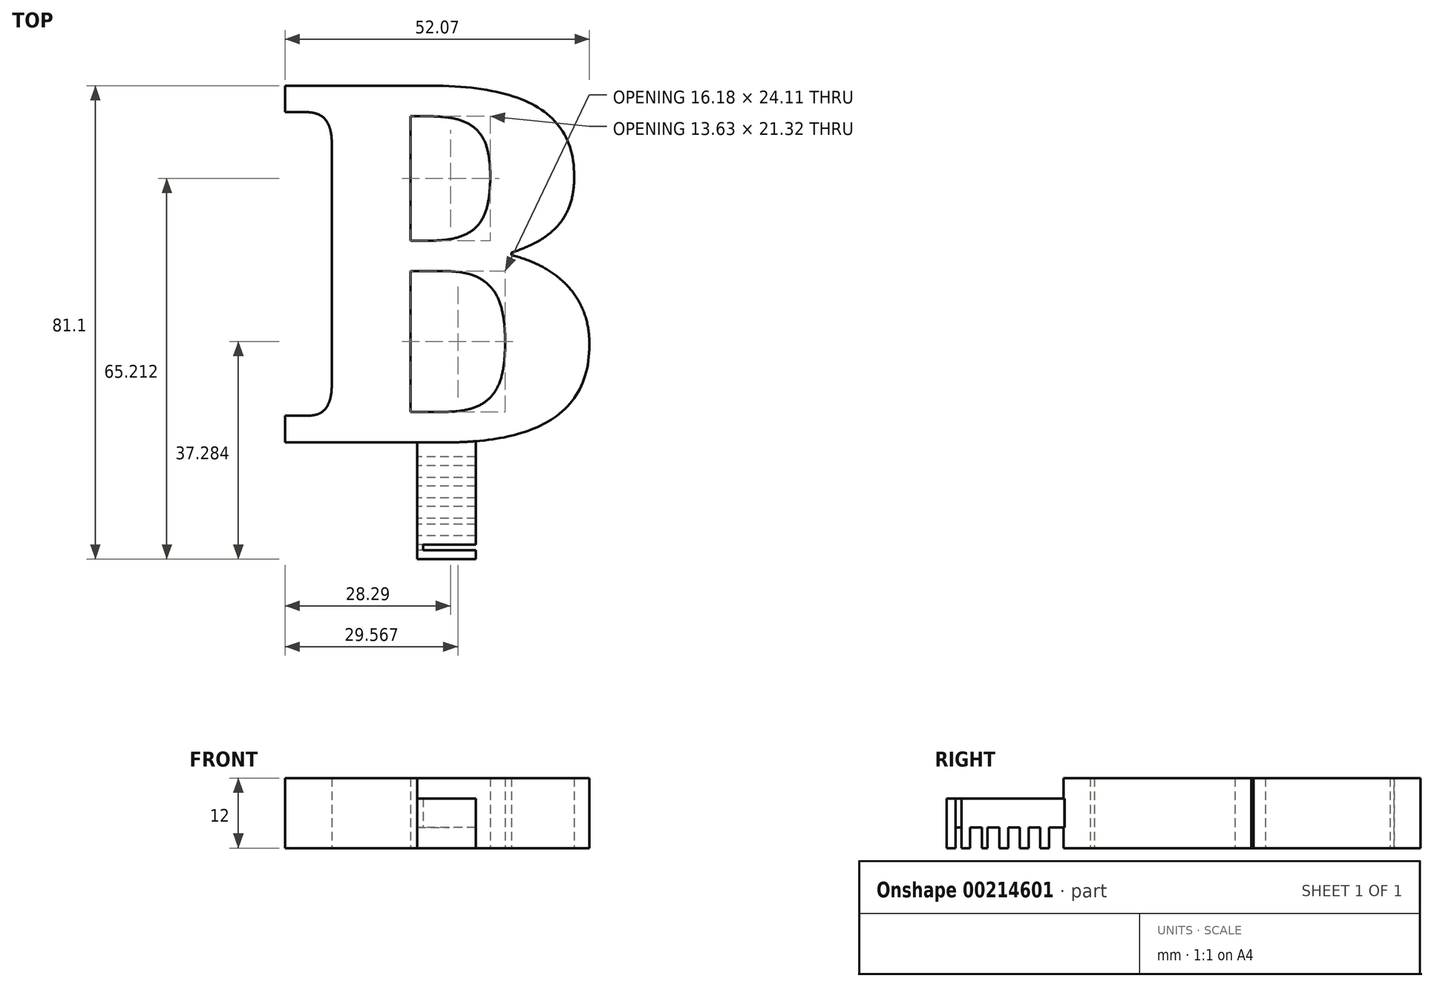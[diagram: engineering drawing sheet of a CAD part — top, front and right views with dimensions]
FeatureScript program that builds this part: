
annotation { "Feature Type Name" : "Feature", "Feature Type Description" : "" }
export const myFeature = defineFeature(function(context is Context, id is Id, definition is map)
    precondition{}
    {
        {
            var Q0;
            Q0=qCreatedBy(makeId("Top.planeOp"),FACE);
            var sketch = newSketch(context, id + "F0", { "sketchPlane" : qUnion([Q0])});
            skText(sketch, "E0", { "text": "B", "fontName": "NotoSerif-Bold.ttf"});
            skLineSegment(sketch, "E1.bottom", {"start": v(-5, -61.62) * mm, "end": v(5, -61.62) * mm});
            skLineSegment(sketch, "E1.top", {"start": v(-5, -81.62) * mm, "end": v(5, -81.62) * mm});
            skLineSegment(sketch, "E1.left", {"start": v(-5, -61.62) * mm, "end": v(-5, -81.62) * mm});
            skLineSegment(sketch, "E1.right", {"start": v(5, -61.62) * mm, "end": v(5, -81.62) * mm});
            skPoint(sketch, "E2", {"position": v(0, -61.62) * mm});
            skLineSegment(sketch, "E3", {"start": v(5, -61.62) * mm, "end": v(5, -61.12) * mm});
            skLineSegment(sketch, "E4.bottom", {"start": v(-4, -62.62) * mm, "end": v(4, -62.62) * mm});
            skLineSegment(sketch, "E4.top", {"start": v(-4, -80.12) * mm, "end": v(4, -80.12) * mm});
            skLineSegment(sketch, "E4.left", {"start": v(-4, -62.62) * mm, "end": v(-4, -80.12) * mm});
            skLineSegment(sketch, "E4.right", {"start": v(4, -62.62) * mm, "end": v(4, -80.12) * mm});
            skPoint(sketch, "E5", {"position": v(0, -80.12) * mm});
            skPoint(sketch, "E6", {"position": v(0, -81.62) * mm});
            skLineSegment(sketch, "E7", {"start": v(-5, -62.62) * mm, "end": v(-4, -62.62) * mm});
            skLineSegment(sketch, "E8", {"start": v(5, -62.62) * mm, "end": v(4, -62.62) * mm});
            skLineSegment(sketch, "E9", {"start": v(4, -80.12) * mm, "end": v(5, -80.12) * mm});
            skLineSegment(sketch, "E10", {"start": v(5, -80.12) * mm, "end": v(-4, -80.12) * mm});
            skLineSegment(sketch, "E11", {"start": v(-5, -80.12) * mm, "end": v(-4, -80.12) * mm});
            skLineSegment(sketch, "E12", {"start": v(-4, -78.12) * mm, "end": v(-5, -78.12) * mm});
            skLineSegment(sketch, "E13", {"start": v(-5, -69.12) * mm, "end": v(-4, -69.12) * mm});
            skLineSegment(sketch, "E14", {"start": v(-4, -69.12) * mm, "end": v(-4, -71.12) * mm});
            skLineSegment(sketch, "E15", {"start": v(-4, -71.12) * mm, "end": v(-5, -71.12) * mm});
            skLineSegment(sketch, "E16.MirrorCS", {"start": v(5, -69.12) * mm, "end": v(4, -69.12) * mm});
            skLineSegment(sketch, "E17.MirrorCS", {"start": v(4, -71.12) * mm, "end": v(5, -71.12) * mm});
            skLineSegment(sketch, "E18.MirrorCS", {"start": v(4, -78.12) * mm, "end": v(5, -78.12) * mm});
            skLineSegment(sketch, "E19.bottom", {"start": v(-5, -77.62) * mm, "end": v(5, -77.62) * mm});
            skLineSegment(sketch, "E19.top", {"start": v(-5, -79.12) * mm, "end": v(5, -79.12) * mm});
            skLineSegment(sketch, "E19.left", {"start": v(-5, -77.62) * mm, "end": v(-5, -79.12) * mm});
            skLineSegment(sketch, "E19.right", {"start": v(5, -77.62) * mm, "end": v(5, -79.12) * mm});
            skPoint(sketch, "E20", {"position": v(0, -79.12) * mm});
            skLineSegment(sketch, "E21.bottom", {"start": v(-5, -74.62) * mm, "end": v(5, -74.62) * mm});
            skLineSegment(sketch, "E21.top", {"start": v(-5, -75.62) * mm, "end": v(5, -75.62) * mm});
            skLineSegment(sketch, "E21.left", {"start": v(-5, -74.62) * mm, "end": v(-5, -75.62) * mm});
            skLineSegment(sketch, "E21.right", {"start": v(5, -74.62) * mm, "end": v(5, -75.62) * mm});
            skPoint(sketch, "E22", {"position": v(0, -75.62) * mm});
            skLineSegment(sketch, "E23.bottom", {"start": v(-5, -71.12) * mm, "end": v(5, -71.12) * mm});
            skLineSegment(sketch, "E23.top", {"start": v(-5, -72.62) * mm, "end": v(5, -72.62) * mm});
            skLineSegment(sketch, "E23.left", {"start": v(-5, -71.12) * mm, "end": v(-5, -72.62) * mm});
            skLineSegment(sketch, "E23.right", {"start": v(5, -71.12) * mm, "end": v(5, -72.62) * mm});
            skPoint(sketch, "E24", {"position": v(0, -72.62) * mm});
            skLineSegment(sketch, "E25.bottom", {"start": v(-5, -67.62) * mm, "end": v(5, -67.62) * mm});
            skLineSegment(sketch, "E25.top", {"start": v(-5, -69.12) * mm, "end": v(5, -69.12) * mm});
            skLineSegment(sketch, "E25.left", {"start": v(-5, -67.62) * mm, "end": v(-5, -69.12) * mm});
            skLineSegment(sketch, "E25.right", {"start": v(5, -67.62) * mm, "end": v(5, -69.12) * mm});
            skPoint(sketch, "E26", {"position": v(0, -69.12) * mm});
            skLineSegment(sketch, "E27.bottom", {"start": v(-5, -64.12) * mm, "end": v(5, -64.12) * mm});
            skLineSegment(sketch, "E27.top", {"start": v(-5, -65.62) * mm, "end": v(5, -65.62) * mm});
            skLineSegment(sketch, "E27.left", {"start": v(-5, -64.12) * mm, "end": v(-5, -65.62) * mm});
            skLineSegment(sketch, "E27.right", {"start": v(5, -64.12) * mm, "end": v(5, -65.62) * mm});
            skPoint(sketch, "E28", {"position": v(0, -65.62) * mm});
            skPoint(sketch, "E29", {"position": v(0, -67.62) * mm});
            const initialGuessF0  = {"E0": [-0.03, -0.06162, 1, 0, 0.06162]};
            skSetInitialGuess(sketch, initialGuessF0);
            skSolve(sketch);
        }
        {
            var Q0;
            Q0=makeQuery(id+"F0.imprint","IMPRINT",FACE,{"disambiguationData":[TD([[makeQuery(id+"F0.imprint","IMPRINT",EDGE,{"derivedFrom":sQuery(id+"F0.wireOp",EDGE,"E0.sketch_text.stroke-0")}),-1.0]])]});
            extrude(context, id + "F1", {"entities" : qUnion([Q0]), "depth" : 12 * mm});
        }
        {
            var Q0;
            {var subQ0=sQuery(id+"F0.wireOp",EDGE,"E1.bottom");var subQ1=sQuery(id+"F0.wireOp",EDGE,"E0.sketch_text.stroke-10");var subQ2=makeQuery(id+"F0.imprint","INTERSECT",VERTEX,{"derivedFrom":[subQ1,subQ0]});Q0=makeQuery(id+"F0.imprint","IMPRINT",FACE,{"disambiguationData":[TD([[makeQuery(id+"F0.imprint","IMPRINT",EDGE,{"disambiguationData":[TD([[subQ2,1.0]])],"derivedFrom":subQ1}),1.0]])]});}
            var Q1;
            Q1=makeQuery(id+"F0.imprint","IMPRINT",FACE,{"disambiguationData":[TD([[makeQuery(id+"F0.imprint","IMPRINT",EDGE,{"derivedFrom":sQuery(id+"F0.wireOp",EDGE,"E1.top")}),1.0]])]});
            var Q2;
            Q2=makeQuery(id+"F0.imprint","IMPRINT",FACE,{"disambiguationData":[TD([[makeQuery(id+"F0.imprint","IMPRINT",EDGE,{"derivedFrom":sQuery(id+"F0.wireOp",EDGE,"E4.bottom")}),1.0]])]});
            var Q3;
            {var subQ0=sQuery(id+"F0.wireOp",EDGE,"E7");Q3=makeQuery(id+"F0.imprint","IMPRINT",FACE,{"disambiguationData":[TD([[makeQuery(id+"F0.imprint","IMPRINT",EDGE,{"derivedFrom":subQ0}),-1.0]])]});}
            var Q4;
            {var subQ5=sQuery(id+"F0.wireOp",EDGE,"E4.bottom");Q4=makeQuery(id+"F0.imprint","IMPRINT",FACE,{"disambiguationData":[TD([[makeQuery(id+"F0.imprint","IMPRINT",EDGE,{"derivedFrom":subQ5}),-1.0]])]});}
            var Q5;
            {var subQ0=sQuery(id+"F0.wireOp",EDGE,"E13");Q5=makeQuery(id+"F0.imprint","IMPRINT",FACE,{"disambiguationData":[TD([[makeQuery(id+"F0.imprint","IMPRINT",EDGE,{"derivedFrom":subQ0}),-1.0]])]});}
            var Q6;
            {var subQ0=sQuery(id+"F0.wireOp",EDGE,"E12");Q6=makeQuery(id+"F0.imprint","IMPRINT",FACE,{"disambiguationData":[TD([[makeQuery(id+"F0.imprint","IMPRINT",EDGE,{"derivedFrom":subQ0}),-1.0]])]});}
            var Q7;
            {var subQ0=sQuery(id+"F0.wireOp",EDGE,"E16.MirrorCS");Q7=makeQuery(id+"F0.imprint","IMPRINT",FACE,{"disambiguationData":[TD([[makeQuery(id+"F0.imprint","IMPRINT",EDGE,{"derivedFrom":subQ0}),1.0]])]});}
            var Q8;
            {var subQ0=sQuery(id+"F0.wireOp",EDGE,"E8");Q8=makeQuery(id+"F0.imprint","IMPRINT",FACE,{"disambiguationData":[TD([[makeQuery(id+"F0.imprint","IMPRINT",EDGE,{"derivedFrom":subQ0}),1.0]])]});}
            var Q9;
            {var subQ0=sQuery(id+"F0.wireOp",EDGE,"E17.MirrorCS");Q9=makeQuery(id+"F0.imprint","IMPRINT",FACE,{"disambiguationData":[TD([[makeQuery(id+"F0.imprint","IMPRINT",EDGE,{"derivedFrom":subQ0}),-1.0]])]});}
            var Q10;
            {var subQ0=sQuery(id+"F0.wireOp",EDGE,"E11");Q10=makeQuery(id+"F0.imprint","IMPRINT",FACE,{"disambiguationData":[TD([[makeQuery(id+"F0.imprint","IMPRINT",EDGE,{"derivedFrom":subQ0}),1.0]])]});}
            var Q11;
            {var subQ3=sQuery(id+"F0.wireOp",EDGE,"E18.MirrorCS");Q11=makeQuery(id+"F0.imprint","IMPRINT",FACE,{"disambiguationData":[TD([[makeQuery(id+"F0.imprint","IMPRINT",EDGE,{"derivedFrom":subQ3}),-1.0]])]});}
            var Q12;
            Q12=makeQuery(id+"F0.imprint","IMPRINT",FACE,{"disambiguationData":[TD([[makeQuery(id+"F0.imprint","IMPRINT",EDGE,{"derivedFrom":sQuery(id+"F0.wireOp",EDGE,"E27.bottom")}),-1.0]])]});
            var Q13;
            Q13=makeQuery(id+"F0.imprint","IMPRINT",FACE,{"disambiguationData":[TD([[makeQuery(id+"F0.imprint","IMPRINT",EDGE,{"derivedFrom":sQuery(id+"F0.wireOp",EDGE,"E25.bottom")}),-1.0]])]});
            var Q14;
            Q14=makeQuery(id+"F0.imprint","IMPRINT",FACE,{"disambiguationData":[TD([[makeQuery(id+"F0.imprint","IMPRINT",EDGE,{"derivedFrom":sQuery(id+"F0.wireOp",EDGE,"E23.bottom")}),-1.0]])]});
            var Q15;
            Q15=makeQuery(id+"F0.imprint","IMPRINT",FACE,{"disambiguationData":[TD([[makeQuery(id+"F0.imprint","IMPRINT",EDGE,{"derivedFrom":sQuery(id+"F0.wireOp",EDGE,"E21.bottom")}),-1.0]])]});
            var Q16;
            Q16=makeQuery(id+"F0.imprint","IMPRINT",FACE,{"disambiguationData":[TD([[makeQuery(id+"F0.imprint","IMPRINT",EDGE,{"derivedFrom":sQuery(id+"F0.wireOp",EDGE,"E19.bottom")}),-1.0]])]});
            var Q17;
            {var subQ3=sQuery(id+"F0.wireOp",EDGE,"E27.top");var subQ5=sQuery(id+"F0.wireOp",EDGE,"E4.left");var subQ6=makeQuery(id+"F0.imprint","INTERSECT",VERTEX,{"derivedFrom":[subQ5,subQ3]});Q17=makeQuery(id+"F0.imprint","IMPRINT",FACE,{"disambiguationData":[TD([[makeQuery(id+"F0.imprint","IMPRINT",EDGE,{"disambiguationData":[TD([[subQ6,-1.0]])],"derivedFrom":subQ5}),-1.0]])]});}
            var Q18;
            {var subQ0=sQuery(id+"F0.wireOp",EDGE,"E27.top");var subQ1=sQuery(id+"F0.wireOp",EDGE,"E4.left");var subQ2=makeQuery(id+"F0.imprint","INTERSECT",VERTEX,{"derivedFrom":[subQ1,subQ0]});Q18=makeQuery(id+"F0.imprint","IMPRINT",FACE,{"disambiguationData":[TD([[makeQuery(id+"F0.imprint","IMPRINT",EDGE,{"disambiguationData":[TD([[subQ2,-1.0]])],"derivedFrom":subQ1}),1.0]])]});}
            var Q19;
            {var subQ3=sQuery(id+"F0.wireOp",EDGE,"E27.top");var subQ5=sQuery(id+"F0.wireOp",EDGE,"E4.right");var subQ6=makeQuery(id+"F0.imprint","INTERSECT",VERTEX,{"derivedFrom":[subQ5,subQ3]});Q19=makeQuery(id+"F0.imprint","IMPRINT",FACE,{"disambiguationData":[TD([[makeQuery(id+"F0.imprint","IMPRINT",EDGE,{"disambiguationData":[TD([[subQ6,-1.0]])],"derivedFrom":subQ5}),1.0]])]});}
            var Q20;
            {var subQ0=sQuery(id+"F0.wireOp",EDGE,"E16.MirrorCS");Q20=makeQuery(id+"F0.imprint","IMPRINT",FACE,{"disambiguationData":[TD([[makeQuery(id+"F0.imprint","IMPRINT",EDGE,{"derivedFrom":subQ0}),-1.0]])]});}
            var Q21;
            {var subQ0=sQuery(id+"F0.wireOp",EDGE,"E13");Q21=makeQuery(id+"F0.imprint","IMPRINT",FACE,{"disambiguationData":[TD([[makeQuery(id+"F0.imprint","IMPRINT",EDGE,{"derivedFrom":subQ0}),1.0]])]});}
            var Q22;
            {var subQ5=sQuery(id+"F0.wireOp",EDGE,"E4.right");var subQ6=makeQuery(id+"F0.imprint","INTERSECT",VERTEX,{"derivedFrom":[subQ5,sQuery(id+"F0.wireOp",EDGE,"E16.MirrorCS")]});Q22=makeQuery(id+"F0.imprint","IMPRINT",FACE,{"disambiguationData":[TD([[makeQuery(id+"F0.imprint","IMPRINT",EDGE,{"disambiguationData":[TD([[subQ6,1.0]])],"derivedFrom":subQ5}),-1.0]])]});}
            var Q23;
            {var subQ3=sQuery(id+"F0.wireOp",EDGE,"E23.top");var subQ5=sQuery(id+"F0.wireOp",EDGE,"E4.left");var subQ6=makeQuery(id+"F0.imprint","INTERSECT",VERTEX,{"derivedFrom":[subQ5,subQ3]});Q23=makeQuery(id+"F0.imprint","IMPRINT",FACE,{"disambiguationData":[TD([[makeQuery(id+"F0.imprint","IMPRINT",EDGE,{"disambiguationData":[TD([[subQ6,-1.0]])],"derivedFrom":subQ5}),-1.0]])]});}
            var Q24;
            {var subQ0=sQuery(id+"F0.wireOp",EDGE,"E15");Q24=makeQuery(id+"F0.imprint","IMPRINT",FACE,{"disambiguationData":[TD([[makeQuery(id+"F0.imprint","IMPRINT",EDGE,{"derivedFrom":subQ0}),1.0]])]});}
            var Q25;
            {var subQ5=sQuery(id+"F0.wireOp",EDGE,"E4.right");var subQ6=makeQuery(id+"F0.imprint","INTERSECT",VERTEX,{"derivedFrom":[subQ5,sQuery(id+"F0.wireOp",EDGE,"E17.MirrorCS")]});Q25=makeQuery(id+"F0.imprint","IMPRINT",FACE,{"disambiguationData":[TD([[makeQuery(id+"F0.imprint","IMPRINT",EDGE,{"disambiguationData":[TD([[subQ6,1.0]])],"derivedFrom":subQ5}),-1.0]])]});}
            var Q26;
            {var subQ3=sQuery(id+"F0.wireOp",EDGE,"E23.top");var subQ5=sQuery(id+"F0.wireOp",EDGE,"E4.right");var subQ6=makeQuery(id+"F0.imprint","INTERSECT",VERTEX,{"derivedFrom":[subQ5,subQ3]});Q26=makeQuery(id+"F0.imprint","IMPRINT",FACE,{"disambiguationData":[TD([[makeQuery(id+"F0.imprint","IMPRINT",EDGE,{"disambiguationData":[TD([[subQ6,-1.0]])],"derivedFrom":subQ5}),1.0]])]});}
            var Q27;
            {var subQ0=sQuery(id+"F0.wireOp",EDGE,"E23.top");var subQ1=sQuery(id+"F0.wireOp",EDGE,"E4.left");var subQ2=makeQuery(id+"F0.imprint","INTERSECT",VERTEX,{"derivedFrom":[subQ1,subQ0]});Q27=makeQuery(id+"F0.imprint","IMPRINT",FACE,{"disambiguationData":[TD([[makeQuery(id+"F0.imprint","IMPRINT",EDGE,{"disambiguationData":[TD([[subQ2,-1.0]])],"derivedFrom":subQ1}),1.0]])]});}
            var Q28;
            {var subQ3=sQuery(id+"F0.wireOp",EDGE,"E21.top");var subQ5=sQuery(id+"F0.wireOp",EDGE,"E4.left");var subQ6=makeQuery(id+"F0.imprint","INTERSECT",VERTEX,{"derivedFrom":[subQ5,subQ3]});Q28=makeQuery(id+"F0.imprint","IMPRINT",FACE,{"disambiguationData":[TD([[makeQuery(id+"F0.imprint","IMPRINT",EDGE,{"disambiguationData":[TD([[subQ6,-1.0]])],"derivedFrom":subQ5}),-1.0]])]});}
            var Q29;
            {var subQ0=sQuery(id+"F0.wireOp",EDGE,"E21.top");var subQ1=sQuery(id+"F0.wireOp",EDGE,"E4.left");var subQ2=makeQuery(id+"F0.imprint","INTERSECT",VERTEX,{"derivedFrom":[subQ1,subQ0]});Q29=makeQuery(id+"F0.imprint","IMPRINT",FACE,{"disambiguationData":[TD([[makeQuery(id+"F0.imprint","IMPRINT",EDGE,{"disambiguationData":[TD([[subQ2,-1.0]])],"derivedFrom":subQ1}),1.0]])]});}
            var Q30;
            {var subQ3=sQuery(id+"F0.wireOp",EDGE,"E21.top");var subQ5=sQuery(id+"F0.wireOp",EDGE,"E4.right");var subQ6=makeQuery(id+"F0.imprint","INTERSECT",VERTEX,{"derivedFrom":[subQ5,subQ3]});Q30=makeQuery(id+"F0.imprint","IMPRINT",FACE,{"disambiguationData":[TD([[makeQuery(id+"F0.imprint","IMPRINT",EDGE,{"disambiguationData":[TD([[subQ6,-1.0]])],"derivedFrom":subQ5}),1.0]])]});}
            var Q31;
            {var subQ0=sQuery(id+"F0.wireOp",EDGE,"E10");var subQ5=sQuery(id+"F0.wireOp",EDGE,"E4.right");var subQ6=makeQuery(id+"F0.imprint","INTERSECT",VERTEX,{"derivedFrom":[subQ5,subQ0]});Q31=makeQuery(id+"F0.imprint","IMPRINT",FACE,{"disambiguationData":[TD([[makeQuery(id+"F0.imprint","IMPRINT",EDGE,{"disambiguationData":[TD([[subQ6,1.0]])],"derivedFrom":subQ5}),-1.0]])]});}
            var Q32;
            {var subQ0=sQuery(id+"F0.wireOp",EDGE,"E10");var subQ5=sQuery(id+"F0.wireOp",EDGE,"E4.right");var subQ6=makeQuery(id+"F0.imprint","INTERSECT",VERTEX,{"derivedFrom":[subQ5,subQ0]});Q32=makeQuery(id+"F0.imprint","IMPRINT",FACE,{"disambiguationData":[TD([[makeQuery(id+"F0.imprint","IMPRINT",EDGE,{"disambiguationData":[TD([[subQ6,1.0]])],"derivedFrom":subQ5}),1.0]])]});}
            var Q33;
            {var subQ6=sQuery(id+"F0.wireOp",EDGE,"E4.left");var subQ7=makeQuery(id+"F0.imprint","INTERSECT",VERTEX,{"derivedFrom":[subQ6,sQuery(id+"F0.wireOp",EDGE,"E12")]});Q33=makeQuery(id+"F0.imprint","IMPRINT",FACE,{"disambiguationData":[TD([[makeQuery(id+"F0.imprint","IMPRINT",EDGE,{"disambiguationData":[TD([[subQ7,1.0]])],"derivedFrom":subQ6}),1.0]])]});}
            var Q34;
            {var subQ0=sQuery(id+"F0.wireOp",EDGE,"E12");Q34=makeQuery(id+"F0.imprint","IMPRINT",FACE,{"disambiguationData":[TD([[makeQuery(id+"F0.imprint","IMPRINT",EDGE,{"derivedFrom":subQ0}),1.0]])]});}
            extrude(context, id + "F2", {"entities" : qUnion([Q0, Q1, Q2, Q3, Q4, Q5, Q6, Q7, Q8, Q9, Q10, Q11, Q12, Q13, Q14, Q15, Q16, Q17, Q18, Q19, Q20, Q21, Q22, Q23, Q24, Q25, Q26, Q27, Q28, Q29, Q30, Q31, Q32, Q33, Q34]), "operationType" : NewBodyOperationType.ADD, "depth" : 8.5 * mm, "hasSecondDirection" : true, "secondDirectionOppositeDirection" : false, "secondDirectionDepth" : 3.5 * mm});
        }
        {
            var Q0;
            {var subQ5=sQuery(id+"F0.wireOp",EDGE,"E1.top");Q0=makeQuery(id+"F0.imprint","IMPRINT",FACE,{"disambiguationData":[TD([[makeQuery(id+"F0.imprint","IMPRINT",EDGE,{"derivedFrom":subQ5}),1.0]])]});}
            var Q1;
            Q1=makeQuery(id+"F0.imprint","IMPRINT",FACE,{"disambiguationData":[TD([[makeQuery(id+"F0.imprint","IMPRINT",EDGE,{"derivedFrom":sQuery(id+"F0.wireOp",EDGE,"E27.bottom")}),-1.0]])]});
            var Q2;
            Q2=makeQuery(id+"F0.imprint","IMPRINT",FACE,{"disambiguationData":[TD([[makeQuery(id+"F0.imprint","IMPRINT",EDGE,{"derivedFrom":sQuery(id+"F0.wireOp",EDGE,"E23.bottom")}),-1.0]])]});
            var Q3;
            Q3=makeQuery(id+"F0.imprint","IMPRINT",FACE,{"disambiguationData":[TD([[makeQuery(id+"F0.imprint","IMPRINT",EDGE,{"derivedFrom":sQuery(id+"F0.wireOp",EDGE,"E25.bottom")}),-1.0]])]});
            var Q4;
            Q4=makeQuery(id+"F0.imprint","IMPRINT",FACE,{"disambiguationData":[TD([[makeQuery(id+"F0.imprint","IMPRINT",EDGE,{"derivedFrom":sQuery(id+"F0.wireOp",EDGE,"E21.bottom")}),-1.0]])]});
            var Q5;
            Q5=makeQuery(id+"F0.imprint","IMPRINT",FACE,{"disambiguationData":[TD([[makeQuery(id+"F0.imprint","IMPRINT",EDGE,{"derivedFrom":sQuery(id+"F0.wireOp",EDGE,"E19.bottom")}),-1.0]])]});
            var Q6;
            {var subQ6=sQuery(id+"F0.wireOp",EDGE,"E4.left");var subQ7=makeQuery(id+"F0.imprint","INTERSECT",VERTEX,{"derivedFrom":[subQ6,sQuery(id+"F0.wireOp",EDGE,"E12")]});Q6=makeQuery(id+"F0.imprint","IMPRINT",FACE,{"disambiguationData":[TD([[makeQuery(id+"F0.imprint","IMPRINT",EDGE,{"disambiguationData":[TD([[subQ7,1.0]])],"derivedFrom":subQ6}),1.0]])]});}
            var Q7;
            {var subQ0=sQuery(id+"F0.wireOp",EDGE,"E18.MirrorCS");Q7=makeQuery(id+"F0.imprint","IMPRINT",FACE,{"disambiguationData":[TD([[makeQuery(id+"F0.imprint","IMPRINT",EDGE,{"derivedFrom":subQ0}),-1.0]])]});}
            var Q8;
            {var subQ0=sQuery(id+"F0.wireOp",EDGE,"E12");Q8=makeQuery(id+"F0.imprint","IMPRINT",FACE,{"disambiguationData":[TD([[makeQuery(id+"F0.imprint","IMPRINT",EDGE,{"derivedFrom":subQ0}),1.0]])]});}
            var Q9;
            {var subQ7=sQuery(id+"F0.wireOp",EDGE,"E4.right");var subQ9=makeQuery(id+"F0.imprint","INTERSECT",VERTEX,{"derivedFrom":[subQ7,sQuery(id+"F0.wireOp",EDGE,"E17.MirrorCS")]});Q9=makeQuery(id+"F0.imprint","IMPRINT",FACE,{"disambiguationData":[TD([[makeQuery(id+"F0.imprint","IMPRINT",EDGE,{"disambiguationData":[TD([[subQ9,1.0]])],"derivedFrom":subQ7}),-1.0]])]});}
            var Q10;
            {var subQ0=sQuery(id+"F0.wireOp",EDGE,"E17.MirrorCS");Q10=makeQuery(id+"F0.imprint","IMPRINT",FACE,{"disambiguationData":[TD([[makeQuery(id+"F0.imprint","IMPRINT",EDGE,{"derivedFrom":subQ0}),-1.0]])]});}
            var Q11;
            {var subQ0=sQuery(id+"F0.wireOp",EDGE,"E15");Q11=makeQuery(id+"F0.imprint","IMPRINT",FACE,{"disambiguationData":[TD([[makeQuery(id+"F0.imprint","IMPRINT",EDGE,{"derivedFrom":subQ0}),1.0]])]});}
            extrude(context, id + "F3", {"entities" : qUnion([Q0, Q1, Q2, Q3, Q4, Q5, Q6, Q7, Q8, Q9, Q10, Q11]), "operationType" : NewBodyOperationType.ADD, "depth" : 8 * mm});
        }
    });
